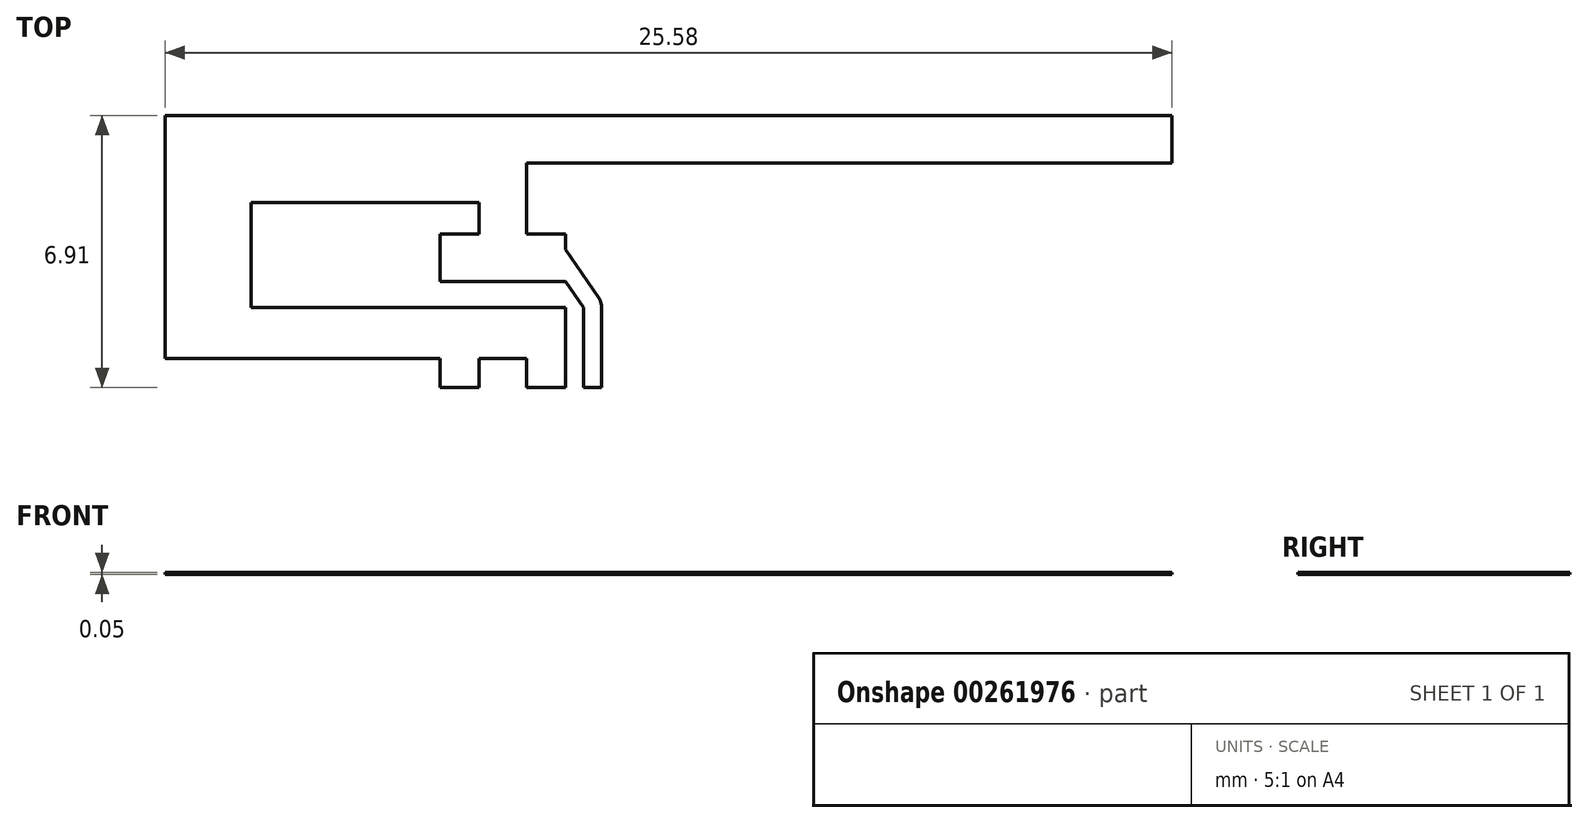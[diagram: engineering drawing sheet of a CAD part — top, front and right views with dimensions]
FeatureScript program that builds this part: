
annotation { "Feature Type Name" : "Feature", "Feature Type Description" : "" }
export const myFeature = defineFeature(function(context is Context, id is Id, definition is map)
    precondition{}
    {
        {
            var Q0;
            Q0=qCreatedBy(makeId("Top.planeOp"),FACE);
            var sketch = newSketch(context, id + "F0", { "sketchPlane" : qUnion([Q0])});
            skLineSegment(sketch, "E0", {"start": v(-0.68, 0) * mm, "end": v(-0.68, 2.03) * mm});
            skLineSegment(sketch, "E1", {"start": v(-0.68, 2.03) * mm, "end": v(-8.68, 2.03) * mm});
            skLineSegment(sketch, "E2", {"start": v(-8.68, 2.03) * mm, "end": v(-8.68, 4.7) * mm});
            skLineSegment(sketch, "E3", {"start": v(-8.68, 4.7) * mm, "end": v(-2.88, 4.7) * mm});
            skLineSegment(sketch, "E4", {"start": v(-2.88, 4.7) * mm, "end": v(-2.88, 3.9) * mm});
            skLineSegment(sketch, "E5", {"start": v(-2.88, 3.9) * mm, "end": v(-3.88, 3.9) * mm});
            skLineSegment(sketch, "E6", {"start": v(-3.88, 3.9) * mm, "end": v(-3.88, 2.69) * mm});
            skLineSegment(sketch, "E7", {"start": v(-3.88, 2.69) * mm, "end": v(-0.68, 2.7) * mm});
            skLineSegment(sketch, "E8", {"start": v(-0.68, 2.69) * mm, "end": v(-0.68, 3.9) * mm});
            skLineSegment(sketch, "E9", {"start": v(-0.68, 3.9) * mm, "end": v(-1.68, 3.9) * mm});
            skLineSegment(sketch, "E10", {"start": v(-1.68, 3.9) * mm, "end": v(-1.68, 5.7) * mm});
            skLineSegment(sketch, "E11", {"start": v(-1.68, 5.7) * mm, "end": v(14.72, 5.7) * mm});
            skLineSegment(sketch, "E12", {"start": v(14.72, 5.7) * mm, "end": v(14.72, 6.91) * mm});
            skLineSegment(sketch, "E13", {"start": v(14.72, 6.91) * mm, "end": v(-10.86, 6.9) * mm});
            skLineSegment(sketch, "E14", {"start": v(-10.86, 6.9) * mm, "end": v(-10.86, 0.74) * mm});
            skLineSegment(sketch, "E15", {"start": v(-10.86, 0.74) * mm, "end": v(-3.88, 0.74) * mm});
            skLineSegment(sketch, "E16", {"start": v(-3.88, 0.74) * mm, "end": v(-3.88, 0) * mm});
            skLineSegment(sketch, "E17", {"start": v(-3.88, 0) * mm, "end": v(-2.88, 0) * mm});
            skLineSegment(sketch, "E18", {"start": v(-2.88, 0) * mm, "end": v(-2.88, 0.74) * mm});
            skLineSegment(sketch, "E19", {"start": v(-2.88, 0.74) * mm, "end": v(-1.68, 0.74) * mm});
            skLineSegment(sketch, "E20", {"start": v(-1.68, 0.74) * mm, "end": v(-1.68, 0) * mm});
            skLineSegment(sketch, "E21", {"start": v(-1.68, 0) * mm, "end": v(-0.68, 0) * mm});
            skLineSegment(sketch, "E22", {"start": v(-0.23, 0) * mm, "end": v(0.23, 0) * mm});
            skLineSegment(sketch, "E23", {"start": v(0.23, 0) * mm, "end": v(0.23, 2.03) * mm});
            skLineSegment(sketch, "E24", {"start": v(0.15, 2.29) * mm, "end": v(-0.68, 3.5) * mm});
            skLineSegment(sketch, "E25", {"start": v(-0.68, 3.5) * mm, "end": v(-0.68, 2.69) * mm});
            skLineSegment(sketch, "E26", {"start": v(-0.23, 0) * mm, "end": v(-0.23, 2.03) * mm});
            skLineSegment(sketch, "E27", {"start": v(-0.23, 2.03) * mm, "end": v(-0.68, 2.69) * mm});
            skLineSegment(sketch, "E28", {"start": v(0.15, 2.29) * mm, "end": v(-0.23, 2.03) * mm});
            skArc(sketch, "E29", {"start": v(0.23, 2.03) * mm, "mid": v(0.2, 2.17) * mm, "end": v(0.15, 2.29) * mm});
            skSolve(sketch);
        }
        {
            var Q0;
            Q0=makeQuery(id+"F0.imprint","IMPRINT",FACE,{"disambiguationData":[TD([[makeQuery(id+"F0.imprint","IMPRINT",EDGE,{"derivedFrom":sQuery(id+"F0.wireOp",EDGE,"E22")}),1.0]])]});
            var Q1;
            Q1=makeQuery(id+"F0.imprint","IMPRINT",FACE,{"disambiguationData":[TD([[makeQuery(id+"F0.imprint","IMPRINT",EDGE,{"derivedFrom":sQuery(id+"F0.wireOp",EDGE,"E0")}),1.0]])]});
            var Q2;
            Q2=makeQuery(id+"F0.imprint","IMPRINT",FACE,{"disambiguationData":[TD([[makeQuery(id+"F0.imprint","IMPRINT",EDGE,{"derivedFrom":sQuery(id+"F0.wireOp",EDGE,"E24")}),1.0]])]});
            extrude(context, id + "F1", {"entities" : qUnion([Q0, Q1, Q2]), "oppositeDirection" : true, "depth" : 0.05 * mm});
        }
    });
